# Revit family: Furniture_Table_Spacestor_Massif-Boardroom
name_source: partatom
category: Furniture
revit_build: Autodesk Revit 2015 (Build: 20140223_1515(x64)
units: mm (PartAtom-declared; Revit-internal decimal feet)

## types (4) — shared parameters
Assembly Code = E2020200
Description = Volute Boardroom Barrel Shaped Table
Height = 755 mm  [stored 2.47703 ft]
Manufacturer = Spacestor
Model = Volute
Table Top Finish = Oak, Red
URL = http://spacestor.uk.com

## per-type parameters (varying)
| type | Boat | Legs Finish | Oval |
| Double D-End | No | Stainless Steel | No |
| Boat-Shaped | Yes | Spacestor Polished Steel | No |
| Oval - Shaped | No | Stainless Steel | Yes |
| Rectangular | No | Stainless Steel | No |

type visibility flags (boolean, named after types; folded from table):
- Double D-End: Yes: Double D-End
- Boat-Shaped: Yes: (none)
- Oval - Shaped: Yes: (none)
- Rectangular: Yes: Rectangular

note: [stored X ft] marks values corroborated as IEEE doubles in the binary element streams (Revit-internal decimal feet)

## geometry (parser evidence)
native form markers: Sweep x18
no freeform markers — native parametric forms only
